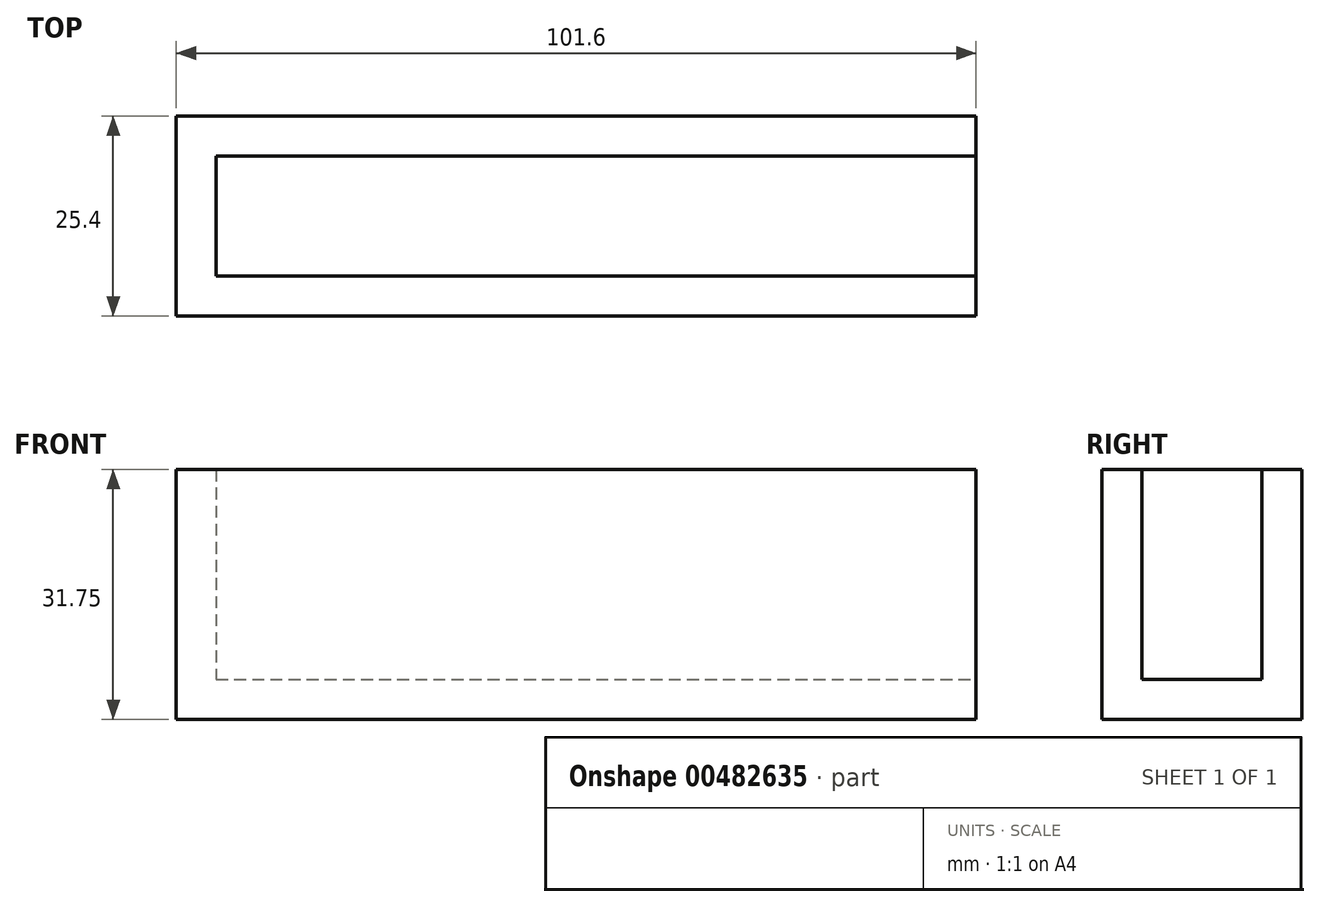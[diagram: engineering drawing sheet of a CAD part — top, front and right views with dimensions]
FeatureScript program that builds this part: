
annotation { "Feature Type Name" : "Feature", "Feature Type Description" : "" }
export const myFeature = defineFeature(function(context is Context, id is Id, definition is map)
    precondition{}
    {
        {
            var Q0;
            Q0=qCreatedBy(makeId("Top.planeOp"),FACE);
            var sketch = newSketch(context, id + "F0", { "sketchPlane" : qUnion([Q0])});
            skLineSegment(sketch, "E0.bottom", {"start": v(-42.42, -45.05) * mm, "end": v(59.18, -45.05) * mm});
            skLineSegment(sketch, "E0.top", {"start": v(-42.42, -70.45) * mm, "end": v(59.18, -70.45) * mm});
            skLineSegment(sketch, "E0.left", {"start": v(-42.42, -45.05) * mm, "end": v(-42.42, -70.45) * mm});
            skLineSegment(sketch, "E0.right", {"start": v(59.18, -45.05) * mm, "end": v(59.18, -70.45) * mm});
            skSolve(sketch);
        }
        {
            var Q0;
            Q0=makeQuery(id+"F0.imprint","IMPRINT",FACE,{"disambiguationData":[TD([[makeQuery(id+"F0.imprint","IMPRINT",EDGE,{"derivedFrom":sQuery(id+"F0.wireOp",EDGE,"E0.bottom")}),-1.0]])]});
            extrude(context, id + "F1", {"entities" : qUnion([Q0]), "depth" : 31.75 * mm});
        }
        {
            var Q0;
            Q0=makeQuery(id+"F1.opExtrude","CAP_FACE",FACE,{"disambiguationData":[OSD([sQuery(id+"F0.wireOp",EDGE,"E0.bottom"),sQuery(id+"F0.wireOp",EDGE,"E0.top"),sQuery(id+"F0.wireOp",EDGE,"E0.left"),sQuery(id+"F0.wireOp",EDGE,"E0.right")])],"isStart":false});
            var Q1;
            Q1=makeQuery(id+"F1.opExtrude","SWEPT_FACE",FACE,{"disambiguationData":[OSD([sQuery(id+"F0.wireOp",EDGE,"E0.right")])]});
            shell(context, id + "F2", {"entities" : qUnion([Q0, Q1]), "thickness" : 5.08 * mm});
        }
    });
